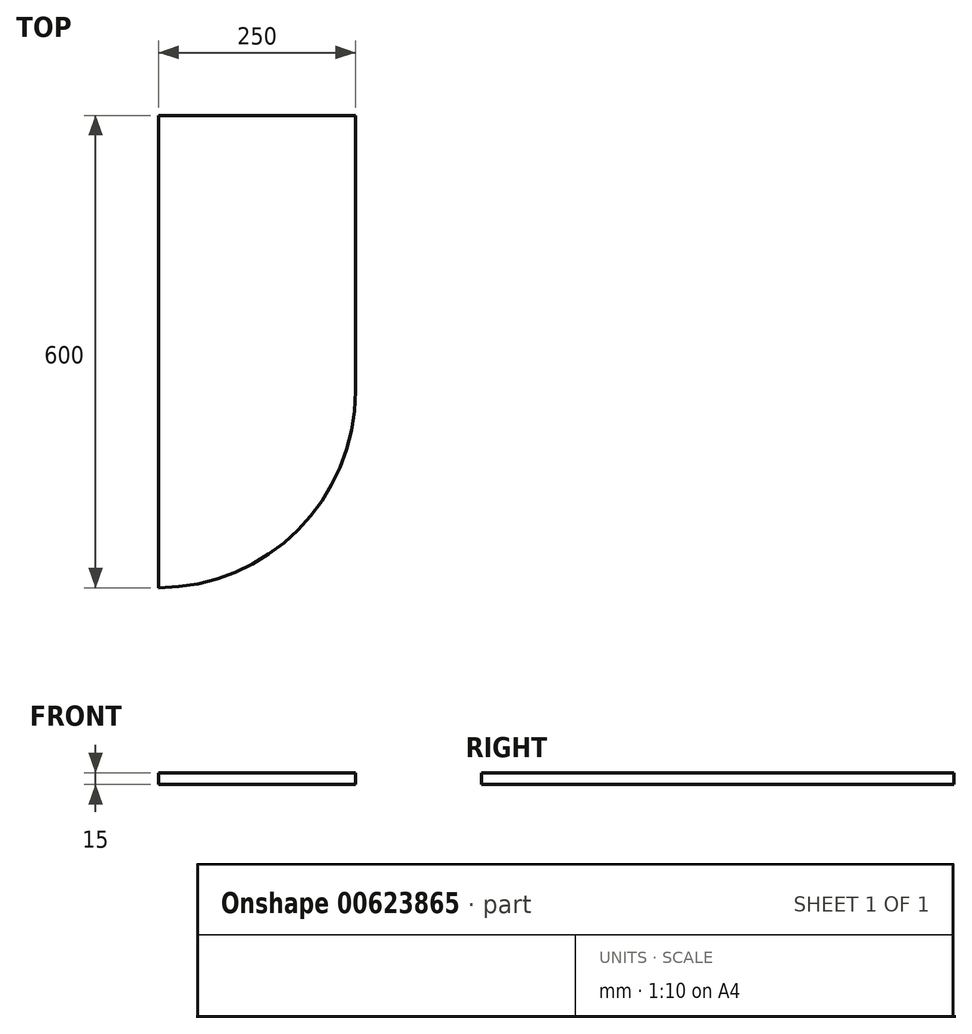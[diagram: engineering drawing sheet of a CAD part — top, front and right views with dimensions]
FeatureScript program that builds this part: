
annotation { "Feature Type Name" : "Feature", "Feature Type Description" : "" }
export const myFeature = defineFeature(function(context is Context, id is Id, definition is map)
    precondition{}
    {
        {
            var Q0;
            Q0=qCreatedBy(makeId("Top.planeOp"),FACE);
            var sketch = newSketch(context, id + "F0", { "sketchPlane" : qUnion([Q0])});
            skLineSegment(sketch, "E0", {"start": v(0, 0) * mm, "end": v(250, 0) * mm});
            skLineSegment(sketch, "E1", {"start": v(250, 0) * mm, "end": v(250, -350) * mm});
            skArc(sketch, "E2", {"start": v(0, -600) * mm, "mid": v(176.78, -526.78) * mm, "end": v(250, -350) * mm});
            skLineSegment(sketch, "E3", {"start": v(0, 0) * mm, "end": v(0, -600) * mm});
            skSolve(sketch);
        }
        {
            var Q0;
            Q0=qSketchRegion(id+"F0",true);
            extrude(context, id + "F1", {"entities" : qUnion([Q0]), "depth" : 15 * mm, "offsetDistance" : 25 * mm});
        }
    });
